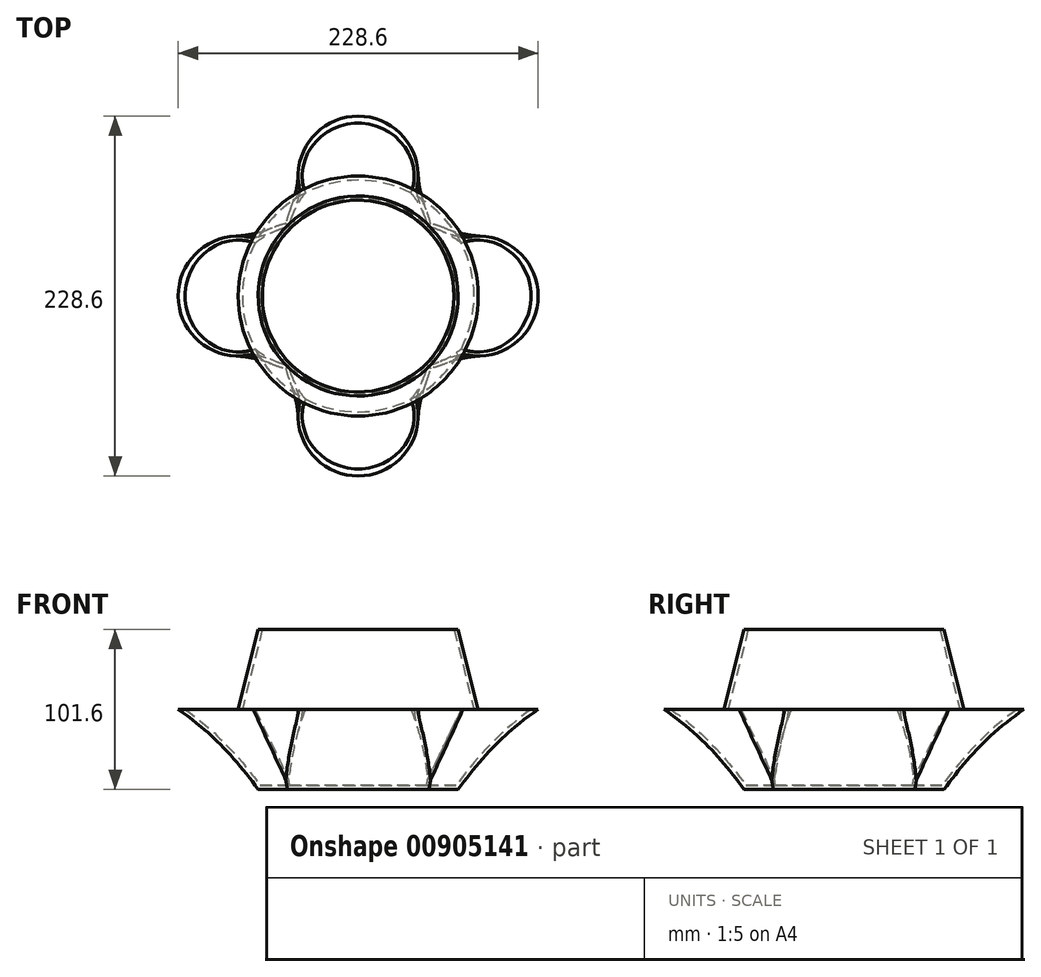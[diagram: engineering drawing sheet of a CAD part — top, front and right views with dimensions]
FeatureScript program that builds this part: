
annotation { "Feature Type Name" : "Feature", "Feature Type Description" : "" }
export const myFeature = defineFeature(function(context is Context, id is Id, definition is map)
    precondition{}
    {
        {
            var Q0;
            Q0=qCreatedBy(makeId("Top.planeOp"),FACE);
            var sketch = newSketch(context, id + "F0", { "sketchPlane" : qUnion([Q0])});
            skCircle(sketch, "E0", {"center": v(0, 0) * mm, "radius": 63.5 * mm});
            skSolve(sketch);
        }
        {
            var Q0;
            Q0=qCreatedBy(makeId("Top.planeOp"),FACE);
            cPlane(context, id + "F1", {"entities" : qUnion([Q0]), "cplaneType" : CPlaneType.OFFSET, "offset" : 50.8 * mm, "width" : 152.4 * mm, "height" : 152.4 * mm});
        }
        {
            var Q0;
            Q0=qCreatedBy(id+"F1.planeOp",FACE);
            var sketch = newSketch(context, id + "F2", { "sketchPlane" : qUnion([Q0])});
            skCircle(sketch, "E1.0", {"center": v(0, 0) * mm, "radius": 76.2 * mm});
            skLineSegment(sketch, "E2", {"start": v(0, 0) * mm, "end": v(0, 76.2) * mm, "construction": true});
            skSolve(sketch);
        }
        {
            var Q0;
            Q0=qCreatedBy(id+"F1.planeOp",FACE);
            var sketch = newSketch(context, id + "F3", { "sketchPlane" : qUnion([Q0])});
            skCircle(sketch, "E3", {"center": v(0, 76.2) * mm, "radius": 38.1 * mm});
            skPoint(sketch, "E4.center", {"position": v(0, 0) * mm});
            skSolve(sketch);
        }
        {
            var Q0;
            Q0=qCreatedBy(id+"F1.planeOp",FACE);
            cPlane(context, id + "F4", {"entities" : qUnion([Q0]), "cplaneType" : CPlaneType.OFFSET, "offset" : 50.8 * mm, "width" : 152.4 * mm, "height" : 152.4 * mm});
        }
        {
            var Q0;
            Q0=qCreatedBy(id+"F4.planeOp",FACE);
            var sketch = newSketch(context, id + "F5", { "sketchPlane" : qUnion([Q0])});
            skCircle(sketch, "E5", {"center": v(0, 0) * mm, "radius": 63.5 * mm});
            skSolve(sketch);
        }
        {
            var Q0;
            Q0=qCreatedBy(makeId("Right.planeOp"),FACE);
            var sketch = newSketch(context, id + "F6", { "sketchPlane" : qUnion([Q0])});
            skLineSegment(sketch, "E6", {"start": v(0, 0) * mm, "end": v(0, 61.82) * mm, "construction": true});
            skSolve(sketch);
        }
        {
            var Q0;
            Q0=makeQuery(id+"F0.imprint","IMPRINT",FACE,{"disambiguationData":[TD([[makeQuery(id+"F0.imprint","IMPRINT",EDGE,{"derivedFrom":sQuery(id+"F0.wireOp",EDGE,"E0")}),1.0]])]});
            var Q1;
            Q1=makeQuery(id+"F3.imprint","IMPRINT",FACE,{"disambiguationData":[TD([[makeQuery(id+"F3.imprint","IMPRINT",EDGE,{"derivedFrom":sQuery(id+"F3.wireOp",EDGE,"E3")}),1.0]])]});
            loft(context, id + "F7", {"sheetProfilesArray" : [{ "sheetProfileEntities" : qUnion([Q0]) }, { "sheetProfileEntities" : qUnion([Q1]) }]});
        }
        {
            var Q0;
            Q0=makeQuery(id+"F7.opLoft","SWEPT_BODY",BODY,{"disambiguationData":[OSD([makeQuery(id+"F0.imprint","IMPRINT",FACE,{"disambiguationData":[TD([[makeQuery(id+"F0.imprint","IMPRINT",EDGE,{"derivedFrom":sQuery(id+"F0.wireOp",EDGE,"E0")}),1.0]])]}),makeQuery(id+"F3.imprint","IMPRINT",FACE,{"disambiguationData":[TD([[makeQuery(id+"F3.imprint","IMPRINT",EDGE,{"derivedFrom":sQuery(id+"F3.wireOp",EDGE,"E3")}),1.0]])]})])]});
            var Q1;
            Q1=sQuery(id+"F6.wireOp",EDGE,"E6");
            circularPattern(context, id + "F8", {"operationType" : NewBodyOperationType.ADD, "entities" : qUnion([Q0]), "axis" : qUnion([Q1]), "angle" : 360 * degree, "instanceCount" : 4, "equalSpace" : true});
        }
        {
            var Q1;
            Q1=makeQuery(id+"F0.imprint","IMPRINT",FACE,{"disambiguationData":[TD([[makeQuery(id+"F0.imprint","IMPRINT",EDGE,{"derivedFrom":sQuery(id+"F0.wireOp",EDGE,"E0")}),1.0]])]});
            var Q2;
            Q2=makeQuery(id+"F2.imprint","IMPRINT",FACE,{"disambiguationData":[TD([[makeQuery(id+"F2.imprint","IMPRINT",EDGE,{"derivedFrom":sQuery(id+"F2.wireOp",EDGE,"E1.0")}),1.0]])]});
            loft(context, id + "F9", {"operationType" : NewBodyOperationType.ADD, "sheetProfilesArray" : [{ "sheetProfileEntities" : qUnion([Q1]) }, { "sheetProfileEntities" : qUnion([Q2]) }]});
        }
        {
            var Q1;
            Q1=makeQuery(id+"F2.imprint","IMPRINT",FACE,{"disambiguationData":[TD([[makeQuery(id+"F2.imprint","IMPRINT",EDGE,{"derivedFrom":sQuery(id+"F2.wireOp",EDGE,"E1.0")}),1.0]])]});
            var Q2;
            Q2=makeQuery(id+"F5.imprint","IMPRINT",FACE,{"disambiguationData":[TD([[makeQuery(id+"F5.imprint","IMPRINT",EDGE,{"derivedFrom":sQuery(id+"F5.wireOp",EDGE,"E5")}),1.0]])]});
            loft(context, id + "F10", {"operationType" : NewBodyOperationType.ADD, "sheetProfilesArray" : [{ "sheetProfileEntities" : qUnion([Q1]) }, { "sheetProfileEntities" : qUnion([Q2]) }]});
        }
        {
            var Q0;
            {var subQ0=sQuery(id+"F3.wireOp",EDGE,"E3");var subQ1=sQuery(id+"F0.wireOp",EDGE,"E0");var subQ2=sQuery(id+"F2.wireOp",EDGE,"E1.0");var subQ3=makeQuery(id+"F7.opLoft","CAP_FACE",FACE,{"disambiguationData":[OSD([makeQuery(id+"F3.imprint","IMPRINT",FACE,{"disambiguationData":[TD([[makeQuery(id+"F3.imprint","IMPRINT",EDGE,{"derivedFrom":subQ0}),1.0]])]})])],"isStart":true});Q0=makeQuery(id+"F10.boolean.opBoolean","SPLIT",FACE,{"disambiguationData":[TD([makeQuery(id+"F8.opPattern","COPY",FACE,{"derivedFrom":makeQuery(id+"F7.opLoft","SWEPT_FACE",FACE,{"disambiguationData":[OSD([subQ1,subQ0])]}),"instanceName":"3"})])],"derivedFrom":makeQuery(id+"F9.boolean.opBoolean","MERGE",FACE,{"derivedFrom":[subQ3,makeQuery(id+"F8.opPattern","COPY",FACE,{"derivedFrom":subQ3,"instanceName":"1"}),makeQuery(id+"F8.opPattern","COPY",FACE,{"derivedFrom":subQ3,"instanceName":"2"}),makeQuery(id+"F8.opPattern","COPY",FACE,{"derivedFrom":subQ3,"instanceName":"3"}),makeQuery(id+"F9.opLoft","CAP_FACE",FACE,{"disambiguationData":[OSD([makeQuery(id+"F2.imprint","IMPRINT",FACE,{"disambiguationData":[TD([[makeQuery(id+"F2.imprint","IMPRINT",EDGE,{"derivedFrom":subQ2}),1.0]])]})])],"isStart":true})]})});}
            var Q1;
            {var subQ0=sQuery(id+"F3.wireOp",EDGE,"E3");var subQ1=sQuery(id+"F0.wireOp",EDGE,"E0");var subQ2=sQuery(id+"F2.wireOp",EDGE,"E1.0");var subQ3=makeQuery(id+"F7.opLoft","CAP_FACE",FACE,{"disambiguationData":[OSD([makeQuery(id+"F3.imprint","IMPRINT",FACE,{"disambiguationData":[TD([[makeQuery(id+"F3.imprint","IMPRINT",EDGE,{"derivedFrom":subQ0}),1.0]])]})])],"isStart":true});Q1=makeQuery(id+"F10.boolean.opBoolean","SPLIT",FACE,{"disambiguationData":[TD([makeQuery(id+"F7.opLoft","SWEPT_FACE",FACE,{"disambiguationData":[OSD([subQ1,subQ0])]})])],"derivedFrom":makeQuery(id+"F9.boolean.opBoolean","MERGE",FACE,{"derivedFrom":[subQ3,makeQuery(id+"F8.opPattern","COPY",FACE,{"derivedFrom":subQ3,"instanceName":"1"}),makeQuery(id+"F8.opPattern","COPY",FACE,{"derivedFrom":subQ3,"instanceName":"2"}),makeQuery(id+"F8.opPattern","COPY",FACE,{"derivedFrom":subQ3,"instanceName":"3"}),makeQuery(id+"F9.opLoft","CAP_FACE",FACE,{"disambiguationData":[OSD([makeQuery(id+"F2.imprint","IMPRINT",FACE,{"disambiguationData":[TD([[makeQuery(id+"F2.imprint","IMPRINT",EDGE,{"derivedFrom":subQ2}),1.0]])]})])],"isStart":true})]})});}
            var Q2;
            {var subQ0=sQuery(id+"F3.wireOp",EDGE,"E3");var subQ1=sQuery(id+"F0.wireOp",EDGE,"E0");var subQ2=sQuery(id+"F2.wireOp",EDGE,"E1.0");var subQ3=makeQuery(id+"F7.opLoft","CAP_FACE",FACE,{"disambiguationData":[OSD([makeQuery(id+"F3.imprint","IMPRINT",FACE,{"disambiguationData":[TD([[makeQuery(id+"F3.imprint","IMPRINT",EDGE,{"derivedFrom":subQ0}),1.0]])]})])],"isStart":true});Q2=makeQuery(id+"F10.boolean.opBoolean","SPLIT",FACE,{"disambiguationData":[TD([makeQuery(id+"F8.opPattern","COPY",FACE,{"derivedFrom":makeQuery(id+"F7.opLoft","SWEPT_FACE",FACE,{"disambiguationData":[OSD([subQ1,subQ0])]}),"instanceName":"1"})])],"derivedFrom":makeQuery(id+"F9.boolean.opBoolean","MERGE",FACE,{"derivedFrom":[subQ3,makeQuery(id+"F8.opPattern","COPY",FACE,{"derivedFrom":subQ3,"instanceName":"1"}),makeQuery(id+"F8.opPattern","COPY",FACE,{"derivedFrom":subQ3,"instanceName":"2"}),makeQuery(id+"F8.opPattern","COPY",FACE,{"derivedFrom":subQ3,"instanceName":"3"}),makeQuery(id+"F9.opLoft","CAP_FACE",FACE,{"disambiguationData":[OSD([makeQuery(id+"F2.imprint","IMPRINT",FACE,{"disambiguationData":[TD([[makeQuery(id+"F2.imprint","IMPRINT",EDGE,{"derivedFrom":subQ2}),1.0]])]})])],"isStart":true})]})});}
            var Q3;
            {var subQ0=sQuery(id+"F3.wireOp",EDGE,"E3");var subQ1=sQuery(id+"F0.wireOp",EDGE,"E0");var subQ2=sQuery(id+"F2.wireOp",EDGE,"E1.0");var subQ3=makeQuery(id+"F7.opLoft","CAP_FACE",FACE,{"disambiguationData":[OSD([makeQuery(id+"F3.imprint","IMPRINT",FACE,{"disambiguationData":[TD([[makeQuery(id+"F3.imprint","IMPRINT",EDGE,{"derivedFrom":subQ0}),1.0]])]})])],"isStart":true});Q3=makeQuery(id+"F10.boolean.opBoolean","SPLIT",FACE,{"disambiguationData":[TD([makeQuery(id+"F8.opPattern","COPY",FACE,{"derivedFrom":makeQuery(id+"F7.opLoft","SWEPT_FACE",FACE,{"disambiguationData":[OSD([subQ1,subQ0])]}),"instanceName":"2"})])],"derivedFrom":makeQuery(id+"F9.boolean.opBoolean","MERGE",FACE,{"derivedFrom":[subQ3,makeQuery(id+"F8.opPattern","COPY",FACE,{"derivedFrom":subQ3,"instanceName":"1"}),makeQuery(id+"F8.opPattern","COPY",FACE,{"derivedFrom":subQ3,"instanceName":"2"}),makeQuery(id+"F8.opPattern","COPY",FACE,{"derivedFrom":subQ3,"instanceName":"3"}),makeQuery(id+"F9.opLoft","CAP_FACE",FACE,{"disambiguationData":[OSD([makeQuery(id+"F2.imprint","IMPRINT",FACE,{"disambiguationData":[TD([[makeQuery(id+"F2.imprint","IMPRINT",EDGE,{"derivedFrom":subQ2}),1.0]])]})])],"isStart":true})]})});}
            var Q4;
            Q4=makeQuery(id+"F10.opLoft","CAP_FACE",FACE,{"disambiguationData":[OSD([makeQuery(id+"F5.imprint","IMPRINT",FACE,{"disambiguationData":[TD([[makeQuery(id+"F5.imprint","IMPRINT",EDGE,{"derivedFrom":sQuery(id+"F5.wireOp",EDGE,"E5")}),1.0]])]})])],"isStart":true});
            shell(context, id + "F11", {"entities" : qUnion([Q0, Q1, Q2, Q3, Q4]), "thickness" : 2.54 * mm});
        }
    });
